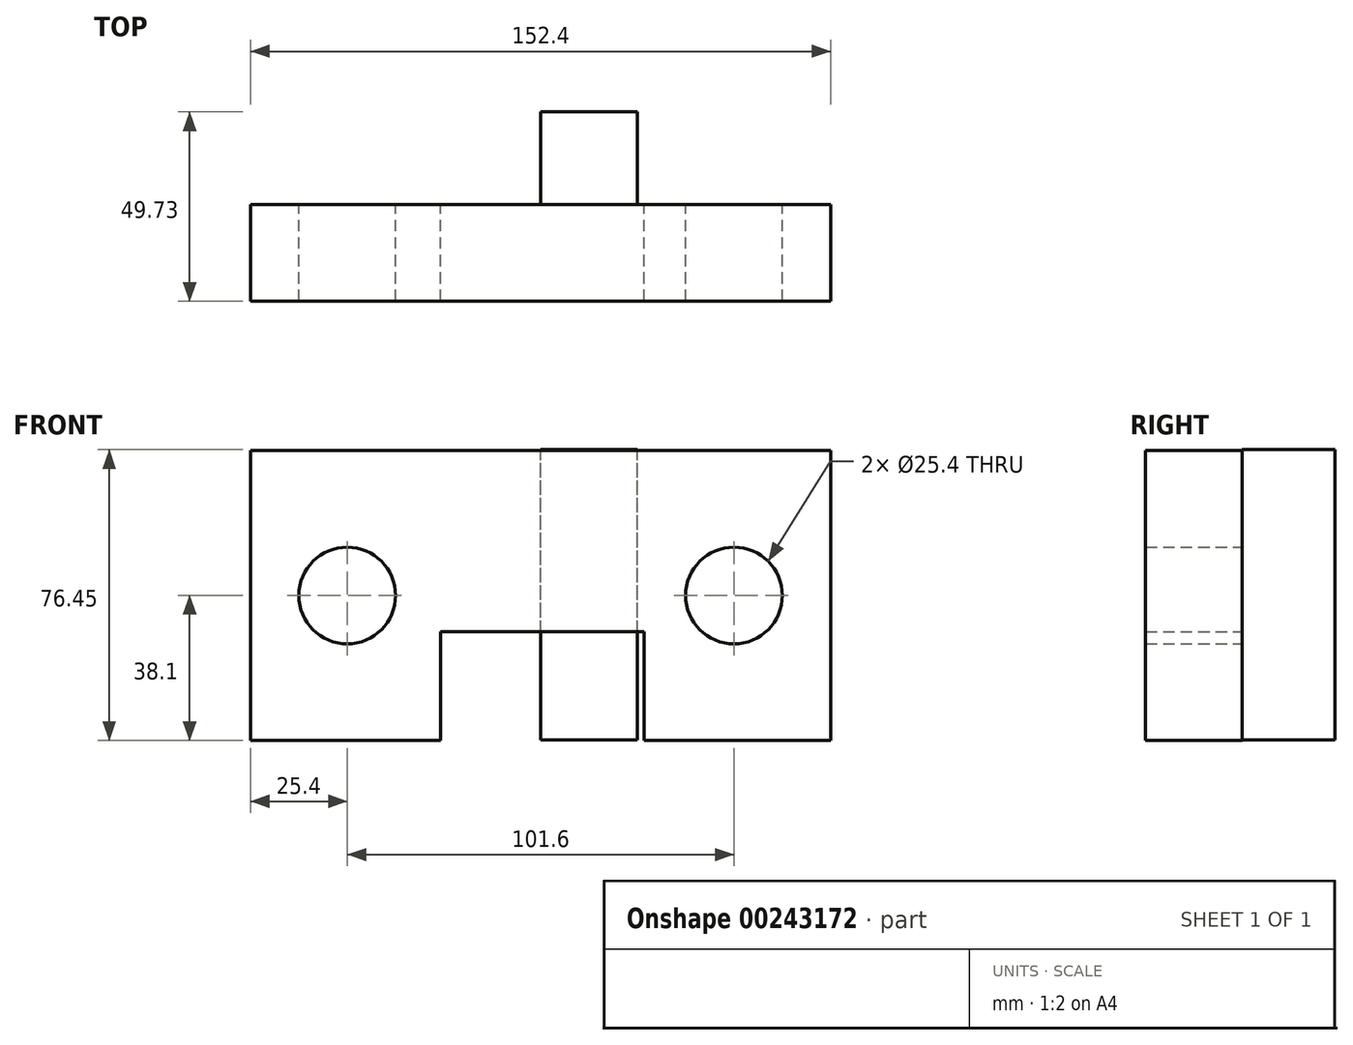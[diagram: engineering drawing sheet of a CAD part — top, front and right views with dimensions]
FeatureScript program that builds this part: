
annotation { "Feature Type Name" : "Feature", "Feature Type Description" : "" }
export const myFeature = defineFeature(function(context is Context, id is Id, definition is map)
    precondition{}
    {
        {
            var Q0;
            Q0=qCreatedBy(makeId("Front.planeOp"),FACE);
            var sketch = newSketch(context, id + "F0", { "sketchPlane" : qUnion([Q0])});
            skLineSegment(sketch, "E0.bottom", {"start": v(-76.2, 38.1) * mm, "end": v(76.2, 38.1) * mm});
            skLineSegment(sketch, "E0.top", {"start": v(-76.2, -38.1) * mm, "end": v(76.2, -38.1) * mm});
            skLineSegment(sketch, "E0.left", {"start": v(-76.2, 38.1) * mm, "end": v(-76.2, -38.1) * mm});
            skLineSegment(sketch, "E0.right", {"start": v(76.2, 38.1) * mm, "end": v(76.2, -38.1) * mm});
            skPoint(sketch, "E0.middle", {"position": v(0, 0) * mm});
            skCircle(sketch, "E1", {"center": v(-50.8, 0) * mm, "radius": 12.7 * mm});
            skCircle(sketch, "E2", {"center": v(50.8, 0) * mm, "radius": 12.7 * mm});
            skLineSegment(sketch, "E3.bottom", {"start": v(-26.33, -38.1) * mm, "end": v(27.13, -38.1) * mm});
            skLineSegment(sketch, "E3.top", {"start": v(-26.33, -9.53) * mm, "end": v(27.13, -9.53) * mm});
            skLineSegment(sketch, "E3.left", {"start": v(-26.33, -38.1) * mm, "end": v(-26.33, -9.52) * mm});
            skLineSegment(sketch, "E3.right", {"start": v(27.13, -38.1) * mm, "end": v(27.13, -9.52) * mm});
            skSolve(sketch);
        }
        {
            var Q0;
            Q0=qCreatedBy(makeId("Right.planeOp"),FACE);
            var sketch = newSketch(context, id + "F1", { "sketchPlane" : qUnion([Q0])});
            skLineSegment(sketch, "E4.bottom", {"start": v(0, -37.98) * mm, "end": v(24.33, -37.98) * mm});
            skLineSegment(sketch, "E4.top", {"start": v(0, 38.35) * mm, "end": v(24.33, 38.35) * mm});
            skLineSegment(sketch, "E4.left", {"start": v(0, -37.98) * mm, "end": v(0, 38.35) * mm});
            skLineSegment(sketch, "E4.right", {"start": v(24.33, -37.98) * mm, "end": v(24.33, 38.35) * mm});
            skSolve(sketch);
        }
        {
            var Q0;
            Q0 = qSketchRegion(id + "F1", true);
            extrude(context, id + "F2", {"entities" : qUnion([Q0]), "depth" : 25.4 * mm});
        }
        {
            var Q0;
            Q0=makeQuery(id+"F0.imprint","IMPRINT",FACE,{"disambiguationData":[TD([[makeQuery(id+"F0.imprint","IMPRINT",EDGE,{"derivedFrom":sQuery(id+"F0.wireOp",EDGE,"E3.bottom")}),1.0]])]});
            var Q1;
            Q1=makeQuery(id+"F0.imprint","IMPRINT",FACE,{"disambiguationData":[TD([[makeQuery(id+"F0.imprint","IMPRINT",EDGE,{"derivedFrom":sQuery(id+"F0.wireOp",EDGE,"E0.bottom")}),-1.0]])]});
            extrude(context, id + "F3", {"entities" : qUnion([Q0, Q1]), "operationType" : NewBodyOperationType.ADD, "depth" : 25.4 * mm});
        }
    });
